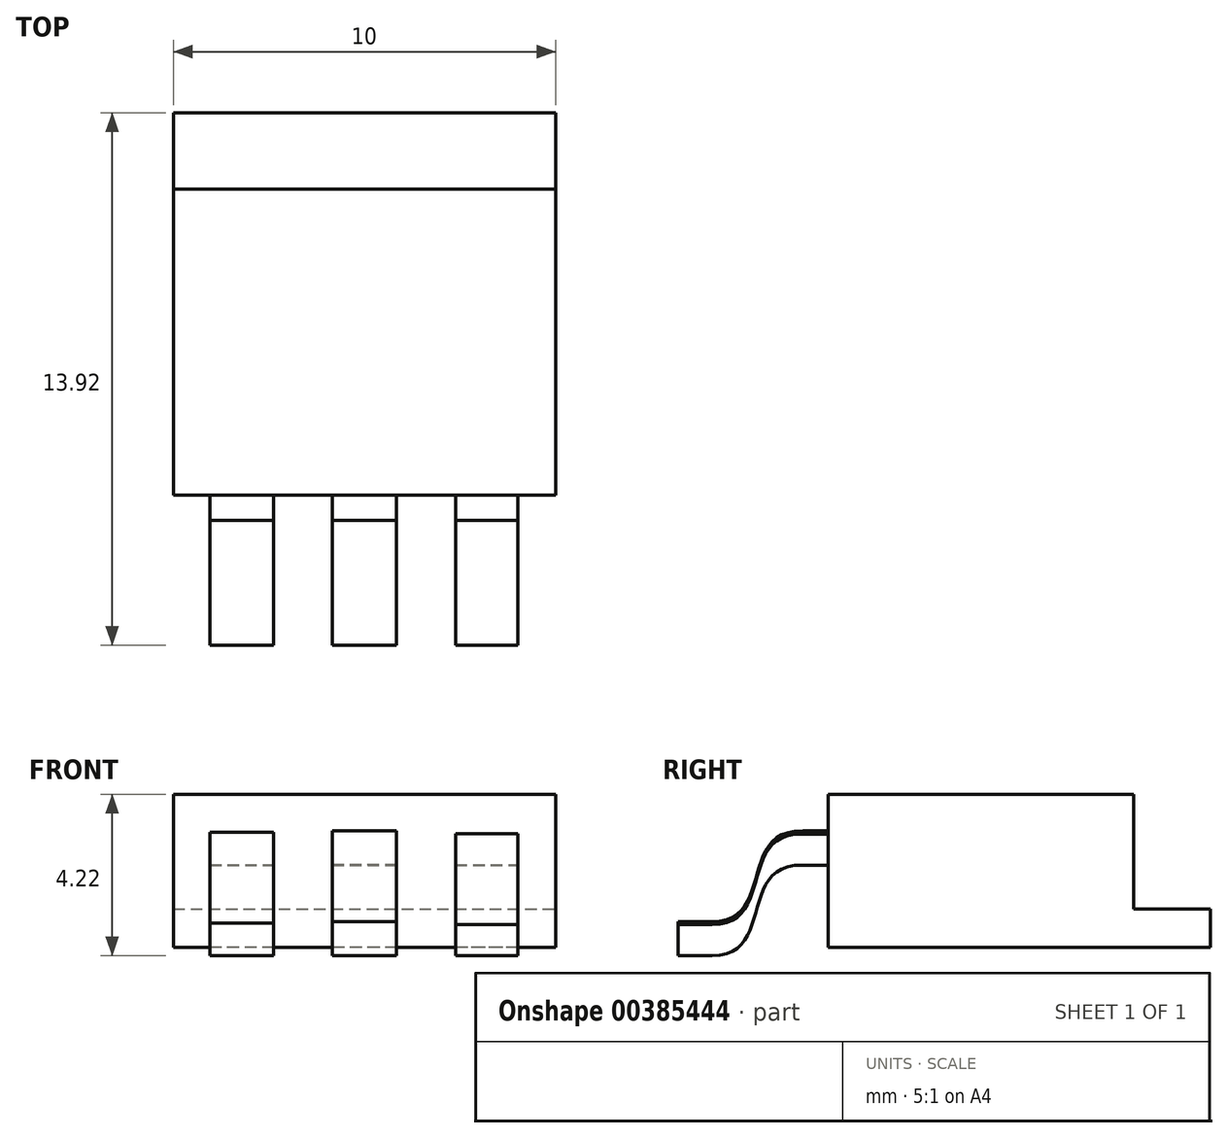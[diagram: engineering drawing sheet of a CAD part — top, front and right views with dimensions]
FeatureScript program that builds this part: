
annotation { "Feature Type Name" : "Feature", "Feature Type Description" : "" }
export const myFeature = defineFeature(function(context is Context, id is Id, definition is map)
    precondition{}
    {
        {
            var Q0;
            Q0=qCreatedBy(makeId("Top.planeOp"),FACE);
            var sketch = newSketch(context, id + "F0", { "sketchPlane" : qUnion([Q0])});
            skLineSegment(sketch, "E0.bottom", {"start": v(5, 5) * mm, "end": v(-5, 5) * mm});
            skLineSegment(sketch, "E0.top", {"start": v(5, -5) * mm, "end": v(-5, -5) * mm});
            skLineSegment(sketch, "E0.left", {"start": v(5, 5) * mm, "end": v(5, -5) * mm});
            skLineSegment(sketch, "E0.right", {"start": v(-5, 5) * mm, "end": v(-5, -5) * mm});
            skPoint(sketch, "E0.middle", {"position": v(0, 0) * mm});
            skSolve(sketch);
        }
        {
            var Q0;
            Q0=makeQuery(id+"F0.imprint","IMPRINT",FACE,{"disambiguationData":[TD([[makeQuery(id+"F0.imprint","IMPRINT",EDGE,{"derivedFrom":sQuery(id+"F0.wireOp",EDGE,"E0.bottom")}),1.0]])]});
            extrude(context, id + "F1", {"entities" : qUnion([Q0]), "depth" : 1 * mm});
        }
        {
            var Q0;
            Q0=makeQuery(id+"F1.opExtrude","CAP_FACE",FACE,{"disambiguationData":[OSD([sQuery(id+"F0.wireOp",EDGE,"E0.bottom"),sQuery(id+"F0.wireOp",EDGE,"E0.top"),sQuery(id+"F0.wireOp",EDGE,"E0.left"),sQuery(id+"F0.wireOp",EDGE,"E0.right")])],"isStart":false});
            var sketch = newSketch(context, id + "F2", { "sketchPlane" : qUnion([Q0])});
            skLineSegment(sketch, "E1.bottom", {"start": v(-5, -5) * mm, "end": v(5, -5) * mm});
            skLineSegment(sketch, "E1.top", {"start": v(-5, 3) * mm, "end": v(5, 3) * mm});
            skLineSegment(sketch, "E1.left", {"start": v(-5, -5) * mm, "end": v(-5, 3) * mm});
            skLineSegment(sketch, "E1.right", {"start": v(5, -5) * mm, "end": v(5, 3) * mm});
            skSolve(sketch);
        }
        {
            var Q0;
            Q0=makeQuery(id+"F2.imprint","IMPRINT",FACE,{"disambiguationData":[TD([[makeQuery(id+"F2.imprint","IMPRINT",EDGE,{"derivedFrom":sQuery(id+"F2.wireOp",EDGE,"E1.bottom")}),-1.0]])]});
            extrude(context, id + "F3", {"entities" : qUnion([Q0]), "operationType" : NewBodyOperationType.ADD, "depth" : 3 * mm});
        }
        {
            var Q0;
            Q0=qCreatedBy(makeId("Right.planeOp"),FACE);
            var sketch = newSketch(context, id + "F4", { "sketchPlane" : qUnion([Q0])});
            skLineSegment(sketch, "E2", {"start": v(-3.6, 2.58) * mm, "end": v(-5.66, 2.58) * mm});
            skFitSpline(sketch, "E3", {"points": [v(-5.66, 2.58) * mm, v(-8.03, 0.2) * mm], "startDerivative": vector(-5.22, 0.07) * mm, "endDerivative": vector(-5, 0) * mm});
            skLineSegment(sketch, "E4", {"start": v(-8.03, 0.2) * mm, "end": v(-8.92, 0.2) * mm});
            skSolve(sketch);
        }
        {
            var Q0;
            Q0=makeQuery(id+"F3.boolean.opBoolean","MERGE",FACE,{"derivedFrom":[makeQuery(id+"F1.opExtrude","SWEPT_FACE",FACE,{"disambiguationData":[OSD([sQuery(id+"F0.wireOp",EDGE,"E0.top")])]}),makeQuery(id+"F3.opExtrude","SWEPT_FACE",FACE,{"disambiguationData":[OSD([sQuery(id+"F2.wireOp",EDGE,"E1.bottom")])]})]});
            var sketch = newSketch(context, id + "F5", { "sketchPlane" : qUnion([Q0])});
            skLineSegment(sketch, "E5.bottom", {"start": v(4, 2.15) * mm, "end": v(2.38, 2.15) * mm});
            skLineSegment(sketch, "E5.top", {"start": v(4, 2.96) * mm, "end": v(2.38, 2.96) * mm});
            skLineSegment(sketch, "E5.left", {"start": v(4, 2.15) * mm, "end": v(4, 2.96) * mm});
            skLineSegment(sketch, "E5.right", {"start": v(2.38, 2.15) * mm, "end": v(2.38, 2.96) * mm});
            skPoint(sketch, "E5.middle", {"position": v(3.2, 2.56) * mm});
            skLineSegment(sketch, "E6.bottom", {"start": v(0.84, 2.15) * mm, "end": v(-0.84, 2.15) * mm});
            skLineSegment(sketch, "E6.top", {"start": v(0.84, 3.05) * mm, "end": v(-0.84, 3.05) * mm});
            skLineSegment(sketch, "E6.left", {"start": v(0.84, 2.15) * mm, "end": v(0.84, 3.05) * mm});
            skLineSegment(sketch, "E6.right", {"start": v(-0.84, 2.15) * mm, "end": v(-0.84, 3.05) * mm});
            skPoint(sketch, "E6.middle", {"position": v(0, 2.6) * mm});
            skLineSegment(sketch, "E7.bottom", {"start": v(-2.37, 2.15) * mm, "end": v(-4.04, 2.15) * mm});
            skLineSegment(sketch, "E7.top", {"start": v(-2.37, 3) * mm, "end": v(-4.04, 3) * mm});
            skLineSegment(sketch, "E7.left", {"start": v(-2.37, 2.15) * mm, "end": v(-2.37, 3) * mm});
            skLineSegment(sketch, "E7.right", {"start": v(-4.04, 2.15) * mm, "end": v(-4.04, 3) * mm});
            skPoint(sketch, "E7.middle", {"position": v(-3.2, 2.58) * mm});
            skSolve(sketch);
        }
        {
            var Q0;
            Q0=makeQuery(id+"F5.imprint","IMPRINT",FACE,{"disambiguationData":[TD([[makeQuery(id+"F5.imprint","IMPRINT",EDGE,{"derivedFrom":sQuery(id+"F5.wireOp",EDGE,"E5.bottom")}),-1.0]])]});
            var Q1;
            Q1=makeQuery(id+"F5.imprint","IMPRINT",FACE,{"disambiguationData":[TD([[makeQuery(id+"F5.imprint","IMPRINT",EDGE,{"derivedFrom":sQuery(id+"F5.wireOp",EDGE,"E6.bottom")}),-1.0]])]});
            var Q2;
            Q2=makeQuery(id+"F5.imprint","IMPRINT",FACE,{"disambiguationData":[TD([[makeQuery(id+"F5.imprint","IMPRINT",EDGE,{"derivedFrom":sQuery(id+"F5.wireOp",EDGE,"E7.bottom")}),-1.0]])]});
            var Q3;
            Q3=sQuery(id+"F4.wireOp",EDGE,"E2");
            var Q4;
            Q4=sQuery(id+"F4.wireOp",EDGE,"E3");
            var Q5;
            Q5=sQuery(id+"F4.wireOp",EDGE,"E4");
            sweep(context, id + "F6", {"operationType" : NewBodyOperationType.ADD, "profiles" : qUnion([Q0, Q1, Q2]), "path" : qUnion([Q3, Q4, Q5]), "keepProfileOrientation" : true});
        }
    });
